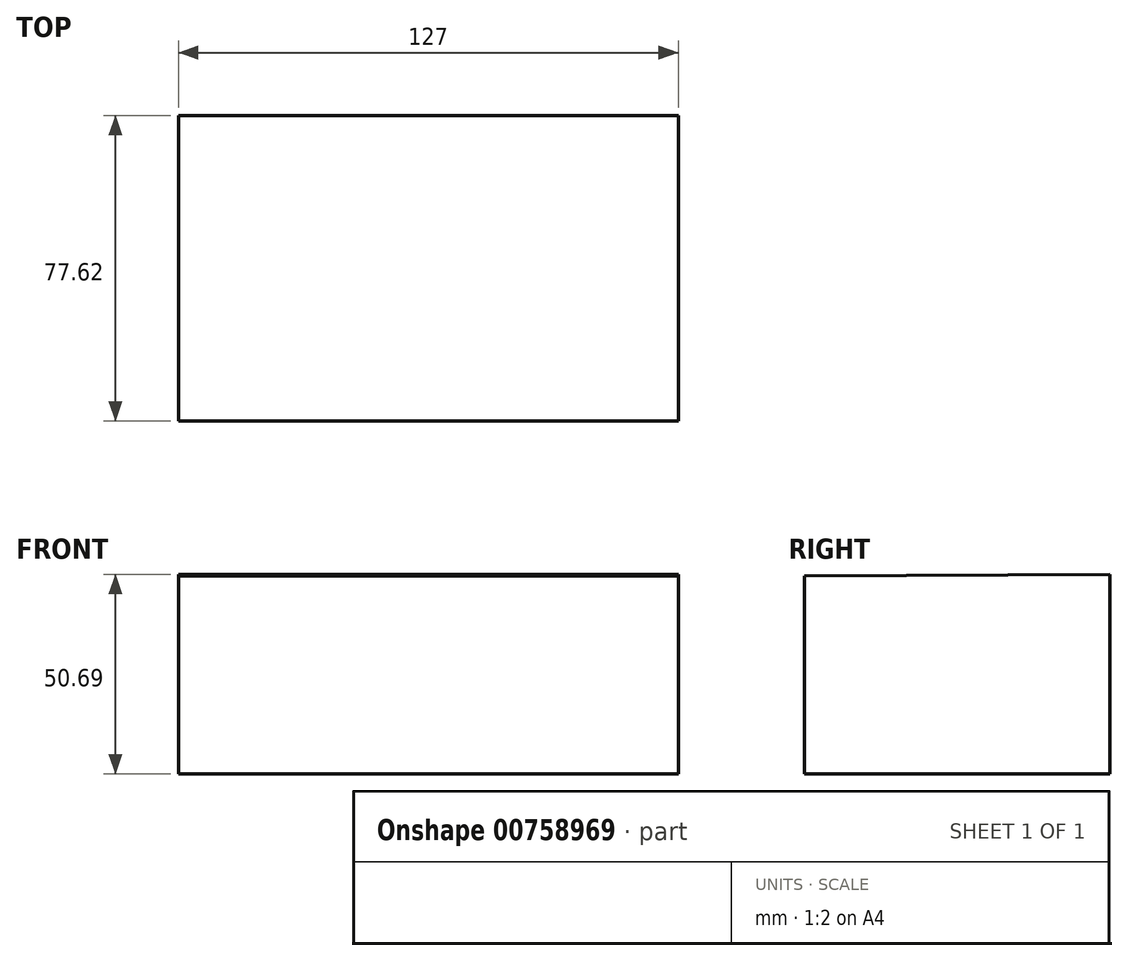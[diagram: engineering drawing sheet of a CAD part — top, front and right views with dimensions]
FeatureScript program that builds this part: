
annotation { "Feature Type Name" : "Feature", "Feature Type Description" : "" }
export const myFeature = defineFeature(function(context is Context, id is Id, definition is map)
    precondition{}
    {
        {
            var Q0;
            Q0=qCreatedBy(makeId("Right.planeOp"),FACE);
            var sketch = newSketch(context, id + "F0", { "sketchPlane" : qUnion([Q0])});
            skLineSegment(sketch, "E0", {"start": v(134.85, 37.23) * mm, "end": v(134.85, -13.46) * mm});
            skLineSegment(sketch, "E1", {"start": v(134.85, -13.46) * mm, "end": v(57.23, -13.46) * mm});
            skLineSegment(sketch, "E2", {"start": v(57.23, -13.46) * mm, "end": v(57.23, 36.83) * mm});
            skLineSegment(sketch, "E3", {"start": v(57.23, 36.83) * mm, "end": v(134.85, 37.23) * mm});
            skSolve(sketch);
        }
        {
            var Q0;
            Q0=makeQuery(id+"F0.imprint","IMPRINT",FACE,{"disambiguationData":[TD([[makeQuery(id+"F0.imprint","IMPRINT",EDGE,{"derivedFrom":sQuery(id+"F0.wireOp",EDGE,"E0")}),-1.0]])]});
            extrude(context, id + "F1", {"entities" : qUnion([Q0]), "depth" : 50.8 * mm, "offsetDistance" : 25.4 * mm, "hasSecondDirection" : true, "secondDirectionOppositeDirection" : true, "secondDirectionDepth" : 76.2 * mm});
        }
    });
